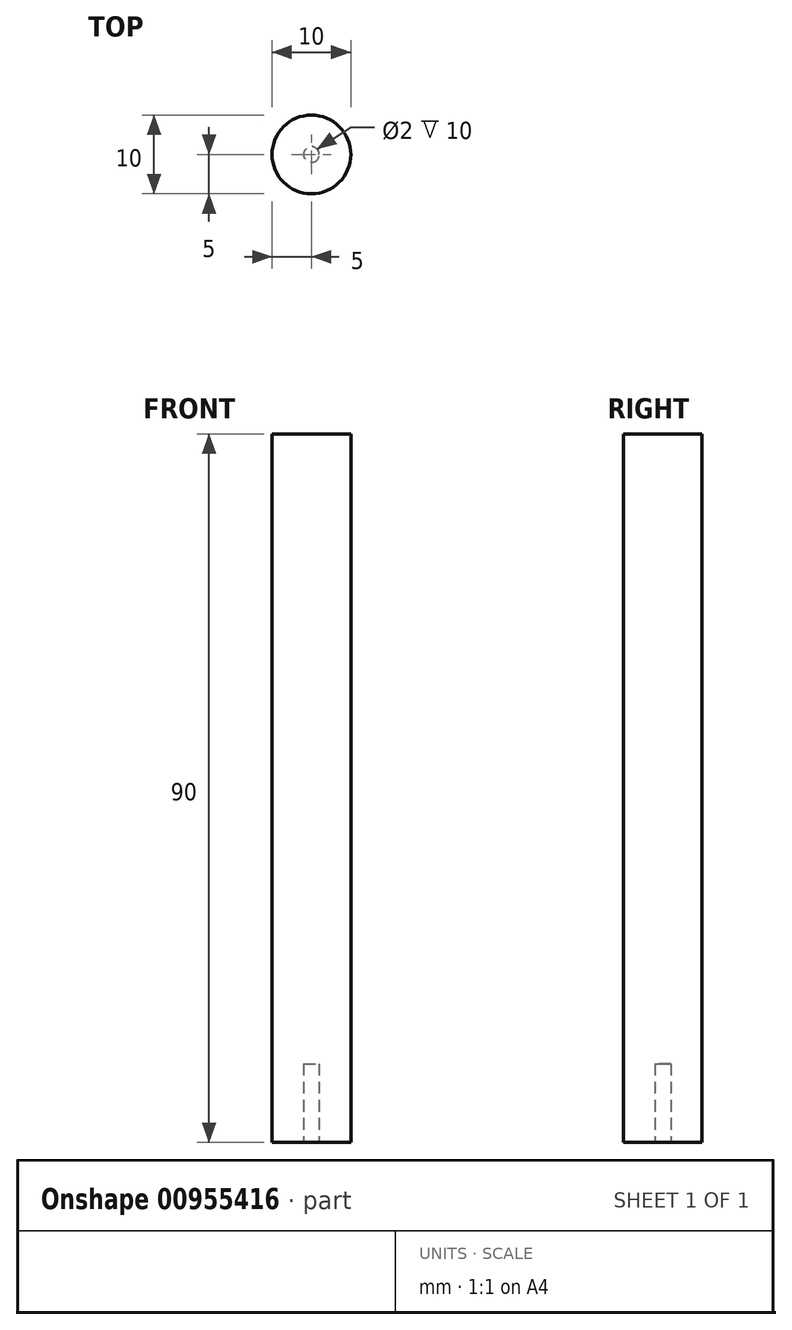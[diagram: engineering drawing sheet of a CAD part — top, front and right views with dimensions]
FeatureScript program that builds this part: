
annotation { "Feature Type Name" : "Feature", "Feature Type Description" : "" }
export const myFeature = defineFeature(function(context is Context, id is Id, definition is map)
    precondition{}
    {
        {
            var Q0;
            Q0=qCreatedBy(makeId("Top.planeOp"),FACE);
            var sketch = newSketch(context, id + "F0", { "sketchPlane" : qUnion([Q0])});
            skCircle(sketch, "E0", {"center": v(0, 0) * mm, "radius": 5 * mm});
            skSolve(sketch);
        }
        {
            var Q0;
            Q0 = qSketchRegion(id + "F0", true);
            extrude(context, id + "F1", {"entities" : qUnion([Q0]), "depth" : 90 * mm, "offsetDistance" : 25 * mm});
        }
        {
            var Q0;
            Q0=makeQuery(id+"F1.opExtrude","CAP_FACE",FACE,{"disambiguationData":[OSD([sQuery(id+"F0.wireOp",EDGE,"E0")])],"isStart":true});
            var sketch = newSketch(context, id + "F2", { "sketchPlane" : qUnion([Q0])});
            skCircle(sketch, "E1", {"center": v(0, 0) * mm, "radius": 1 * mm});
            skSolve(sketch);
        }
        {
            var Q0;
            Q0 = qSketchRegion(id + "F2", true);
            var Q1;
            Q1=sQuery(id+"F2.wireOp",EDGE,"E1");
            extrude(context, id + "F3", {"entities" : qUnion([Q0]), "operationType" : NewBodyOperationType.REMOVE, "surfaceEntities" : qUnion([Q1]), "oppositeDirection" : true, "depth" : 10 * mm, "offsetDistance" : 25 * mm});
        }
    });
